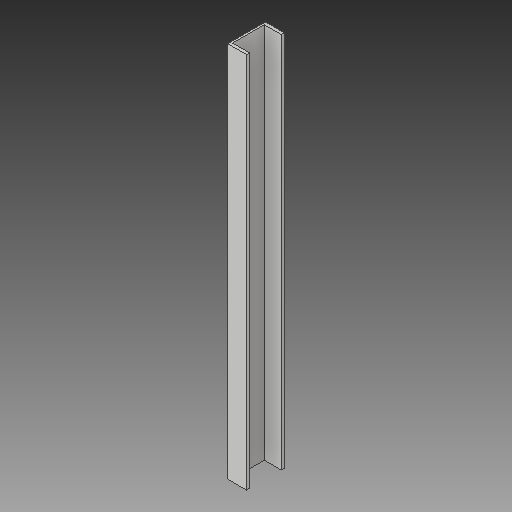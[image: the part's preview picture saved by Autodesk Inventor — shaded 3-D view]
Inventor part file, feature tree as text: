
AUTODESK INVENTOR PART (.ipt)
format: ipt  version: 2019 (Build 230136000, 136)  size: 91,648 bytes
history: native  units: in
note: dims shown in document units (in); Inventor stores cm internally (conversion verified against a paired STEP export)
features: other x3, sketch x1
ambient origin geometry x8: Origin, YZ Plane, XZ Plane, XY Plane, X Axis, Y Axis, Z Axis, Center Point
bodies: Solid1 (feature_tree)
feature tree (4):
  other  "Channel1.ipt"
  other  "Solid1::Channel1.ipt"
  other  "TaggingFeature1"
  sketch  "Sketch1"  dims[d0=0.3937in]
